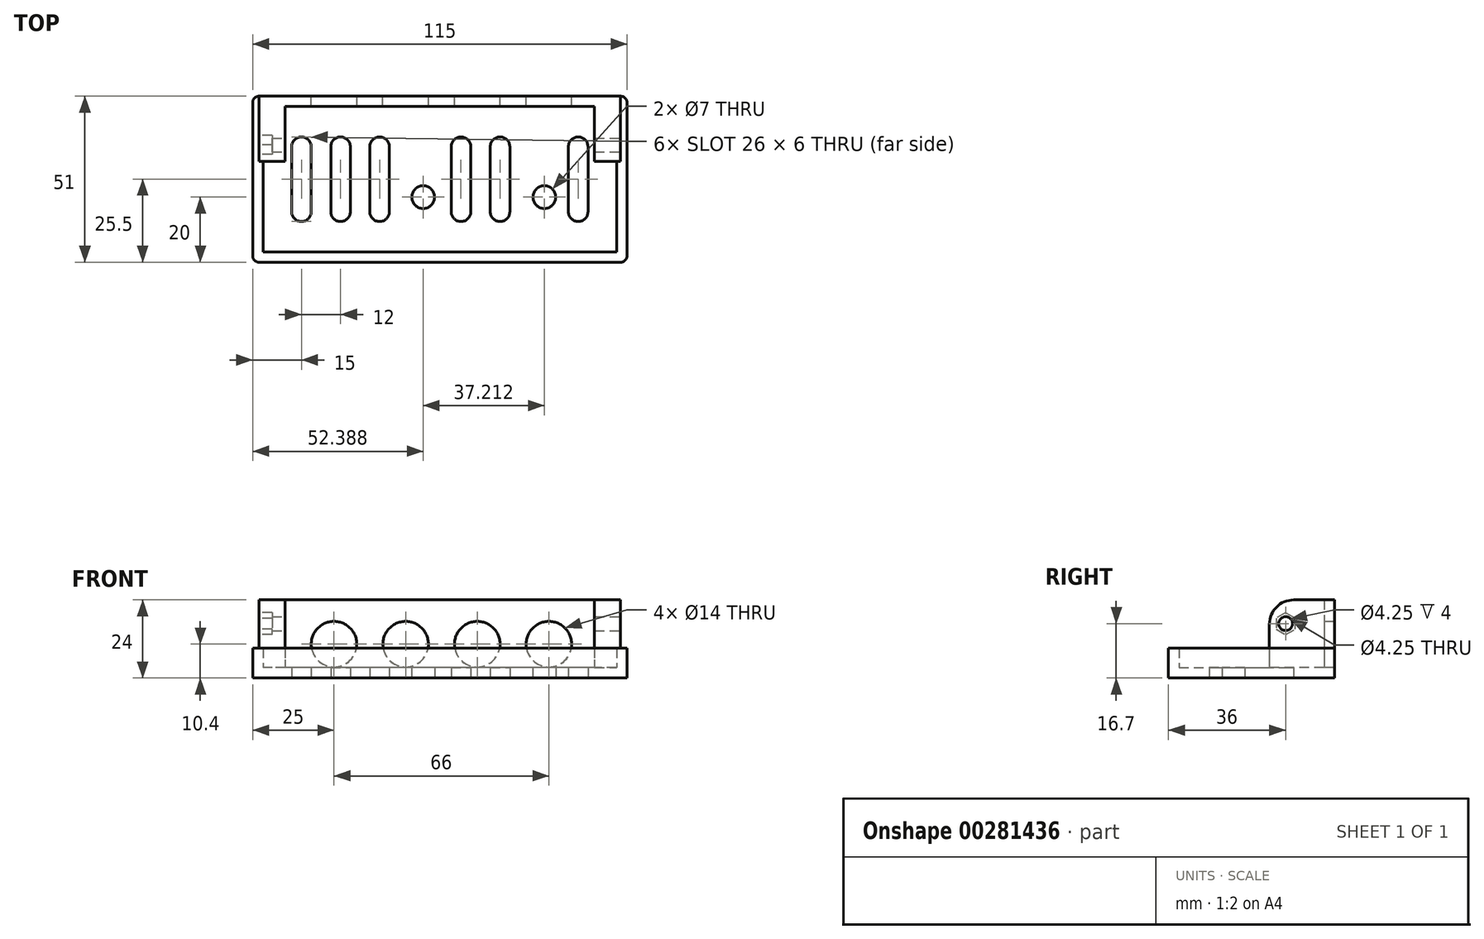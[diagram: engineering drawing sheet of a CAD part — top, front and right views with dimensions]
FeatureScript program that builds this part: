
annotation { "Feature Type Name" : "Feature", "Feature Type Description" : "" }
export const myFeature = defineFeature(function(context is Context, id is Id, definition is map)
    precondition{}
    {
        {
            var Q0;
            Q0=qCreatedBy(makeId("Top.planeOp"),FACE);
            var sketch = newSketch(context, id + "F0", { "sketchPlane" : qUnion([Q0])});
            skLineSegment(sketch, "E0.bottom", {"start": v(57.5, -25.5) * mm, "end": v(-57.5, -25.5) * mm});
            skLineSegment(sketch, "E0.top", {"start": v(57.5, 25.5) * mm, "end": v(-57.5, 25.5) * mm});
            skLineSegment(sketch, "E0.left", {"start": v(57.5, -25.5) * mm, "end": v(57.5, 25.5) * mm});
            skLineSegment(sketch, "E0.right", {"start": v(-57.5, -25.5) * mm, "end": v(-57.5, 25.5) * mm});
            skPoint(sketch, "E0.middle", {"position": v(0, 0) * mm});
            skLineSegment(sketch, "E1.bottom", {"start": v(-42.5, -13) * mm, "end": v(-42.5, -13) * mm});
            skLineSegment(sketch, "E1.top", {"start": v(-42.5, 13) * mm, "end": v(-42.5, 13) * mm});
            skLineSegment(sketch, "E1.left", {"start": v(-39.5, -10) * mm, "end": v(-39.5, 10) * mm});
            skLineSegment(sketch, "E1.right", {"start": v(-45.5, -10) * mm, "end": v(-45.5, 10) * mm});
            skPoint(sketch, "E1.middle", {"position": v(-42.5, 0) * mm});
            skLineSegment(sketch, "E2.bottom", {"start": v(-30.5, -13) * mm, "end": v(-30.5, -13) * mm});
            skLineSegment(sketch, "E2.top", {"start": v(-30.5, 13) * mm, "end": v(-30.5, 13) * mm});
            skLineSegment(sketch, "E2.left", {"start": v(-27.5, -10) * mm, "end": v(-27.5, 10) * mm});
            skLineSegment(sketch, "E2.right", {"start": v(-33.5, -10) * mm, "end": v(-33.5, 10) * mm});
            skPoint(sketch, "E2.middle", {"position": v(-30.5, 0) * mm});
            skLineSegment(sketch, "E3.bottom", {"start": v(-18.5, -13) * mm, "end": v(-18.5, -13) * mm});
            skLineSegment(sketch, "E3.top", {"start": v(-18.5, 13) * mm, "end": v(-18.5, 13) * mm});
            skLineSegment(sketch, "E3.left", {"start": v(-15.5, -10) * mm, "end": v(-15.5, 10) * mm});
            skLineSegment(sketch, "E3.right", {"start": v(-21.5, -10) * mm, "end": v(-21.5, 10) * mm});
            skPoint(sketch, "E3.middle", {"position": v(-18.5, 0) * mm});
            skLineSegment(sketch, "E4.bottom", {"start": v(6.5, -13) * mm, "end": v(6.5, -13) * mm});
            skLineSegment(sketch, "E4.top", {"start": v(6.5, 13) * mm, "end": v(6.5, 13) * mm});
            skLineSegment(sketch, "E4.left", {"start": v(9.5, -10) * mm, "end": v(9.5, 10) * mm});
            skLineSegment(sketch, "E4.right", {"start": v(3.5, -10) * mm, "end": v(3.5, 10) * mm});
            skPoint(sketch, "E4.middle", {"position": v(6.5, 0) * mm});
            skLineSegment(sketch, "E5.bottom", {"start": v(18.5, -13) * mm, "end": v(18.5, -13) * mm});
            skLineSegment(sketch, "E5.top", {"start": v(18.5, 13) * mm, "end": v(18.5, 13) * mm});
            skLineSegment(sketch, "E5.left", {"start": v(21.5, -10) * mm, "end": v(21.5, 10) * mm});
            skLineSegment(sketch, "E5.right", {"start": v(15.5, -10) * mm, "end": v(15.5, 10) * mm});
            skPoint(sketch, "E5.middle", {"position": v(18.5, 0) * mm});
            skLineSegment(sketch, "E6.bottom", {"start": v(42.5, -13) * mm, "end": v(42.5, -13) * mm});
            skLineSegment(sketch, "E6.top", {"start": v(42.5, 13) * mm, "end": v(42.5, 13) * mm});
            skLineSegment(sketch, "E6.left", {"start": v(45.5, -10) * mm, "end": v(45.5, 10) * mm});
            skLineSegment(sketch, "E6.right", {"start": v(39.5, -10) * mm, "end": v(39.5, 10) * mm});
            skPoint(sketch, "E6.middle", {"position": v(42.5, 0) * mm});
            skCircle(sketch, "E7", {"center": v(32.1, -5.5) * mm, "radius": 3.5 * mm});
            skCircle(sketch, "E8", {"center": v(-5.11, -5.5) * mm, "radius": 3.5 * mm});
            skPoint(sketch, "E9.visualSharp", {"position": v(-45.5, 13) * mm});
            skArc(sketch, "E9.filletArc", {"start": v(-42.5, 13) * mm, "mid": v(-44.62, 12.12) * mm, "end": v(-45.5, 10) * mm});
            skPoint(sketch, "E10.visualSharp", {"position": v(-39.5, 13) * mm});
            skArc(sketch, "E10.filletArc", {"start": v(-39.5, 10) * mm, "mid": v(-40.38, 12.12) * mm, "end": v(-42.5, 13) * mm});
            skPoint(sketch, "E11.visualSharp", {"position": v(-39.5, -13) * mm});
            skArc(sketch, "E11.filletArc", {"start": v(-42.5, -13) * mm, "mid": v(-40.38, -12.12) * mm, "end": v(-39.5, -10) * mm});
            skPoint(sketch, "E12.visualSharp", {"position": v(-45.5, -13) * mm});
            skArc(sketch, "E12.filletArc", {"start": v(-45.5, -10) * mm, "mid": v(-44.62, -12.12) * mm, "end": v(-42.5, -13) * mm});
            skPoint(sketch, "E13.visualSharp", {"position": v(-33.5, -13) * mm});
            skArc(sketch, "E13.filletArc", {"start": v(-33.5, -10) * mm, "mid": v(-32.62, -12.12) * mm, "end": v(-30.5, -13) * mm});
            skPoint(sketch, "E14.visualSharp", {"position": v(-27.5, -13) * mm});
            skArc(sketch, "E14.filletArc", {"start": v(-30.5, -13) * mm, "mid": v(-28.38, -12.12) * mm, "end": v(-27.5, -10) * mm});
            skPoint(sketch, "E15.visualSharp", {"position": v(-27.5, 13) * mm});
            skArc(sketch, "E15.filletArc", {"start": v(-27.5, 10) * mm, "mid": v(-28.38, 12.12) * mm, "end": v(-30.5, 13) * mm});
            skPoint(sketch, "E16.visualSharp", {"position": v(-33.5, 13) * mm});
            skArc(sketch, "E16.filletArc", {"start": v(-30.5, 13) * mm, "mid": v(-32.62, 12.12) * mm, "end": v(-33.5, 10) * mm});
            skPoint(sketch, "E17.visualSharp", {"position": v(-21.5, 13) * mm});
            skArc(sketch, "E17.filletArc", {"start": v(-18.5, 13) * mm, "mid": v(-20.62, 12.12) * mm, "end": v(-21.5, 10) * mm});
            skPoint(sketch, "E18.visualSharp", {"position": v(-15.5, 13) * mm});
            skArc(sketch, "E18.filletArc", {"start": v(-15.5, 10) * mm, "mid": v(-16.38, 12.12) * mm, "end": v(-18.5, 13) * mm});
            skPoint(sketch, "E19.visualSharp", {"position": v(-15.5, -13) * mm});
            skArc(sketch, "E19.filletArc", {"start": v(-18.5, -13) * mm, "mid": v(-16.38, -12.12) * mm, "end": v(-15.5, -10) * mm});
            skPoint(sketch, "E20.visualSharp", {"position": v(-21.5, -13) * mm});
            skArc(sketch, "E20.filletArc", {"start": v(-21.5, -10) * mm, "mid": v(-20.62, -12.12) * mm, "end": v(-18.5, -13) * mm});
            skPoint(sketch, "E21.visualSharp", {"position": v(3.5, -13) * mm});
            skArc(sketch, "E21.filletArc", {"start": v(3.5, -10) * mm, "mid": v(4.38, -12.12) * mm, "end": v(6.5, -13) * mm});
            skPoint(sketch, "E22.visualSharp", {"position": v(9.5, -13) * mm});
            skArc(sketch, "E22.filletArc", {"start": v(6.5, -13) * mm, "mid": v(8.62, -12.12) * mm, "end": v(9.5, -10) * mm});
            skPoint(sketch, "E23.visualSharp", {"position": v(9.5, 13) * mm});
            skArc(sketch, "E23.filletArc", {"start": v(9.5, 10) * mm, "mid": v(8.62, 12.12) * mm, "end": v(6.5, 13) * mm});
            skPoint(sketch, "E24.visualSharp", {"position": v(3.5, 13) * mm});
            skArc(sketch, "E24.filletArc", {"start": v(6.5, 13) * mm, "mid": v(4.38, 12.12) * mm, "end": v(3.5, 10) * mm});
            skPoint(sketch, "E25.visualSharp", {"position": v(15.5, -13) * mm});
            skArc(sketch, "E25.filletArc", {"start": v(15.5, -10) * mm, "mid": v(16.38, -12.12) * mm, "end": v(18.5, -13) * mm});
            skPoint(sketch, "E26.visualSharp", {"position": v(21.5, -13) * mm});
            skArc(sketch, "E26.filletArc", {"start": v(18.5, -13) * mm, "mid": v(20.62, -12.12) * mm, "end": v(21.5, -10) * mm});
            skPoint(sketch, "E27.visualSharp", {"position": v(21.5, 13) * mm});
            skArc(sketch, "E27.filletArc", {"start": v(21.5, 10) * mm, "mid": v(20.62, 12.12) * mm, "end": v(18.5, 13) * mm});
            skPoint(sketch, "E28.visualSharp", {"position": v(15.5, 13) * mm});
            skArc(sketch, "E28.filletArc", {"start": v(18.5, 13) * mm, "mid": v(16.38, 12.12) * mm, "end": v(15.5, 10) * mm});
            skPoint(sketch, "E29.visualSharp", {"position": v(39.5, -13) * mm});
            skArc(sketch, "E29.filletArc", {"start": v(39.5, -10) * mm, "mid": v(40.38, -12.12) * mm, "end": v(42.5, -13) * mm});
            skPoint(sketch, "E30.visualSharp", {"position": v(45.5, 13) * mm});
            skArc(sketch, "E30.filletArc", {"start": v(45.5, 10) * mm, "mid": v(44.62, 12.12) * mm, "end": v(42.5, 13) * mm});
            skPoint(sketch, "E31.visualSharp", {"position": v(39.5, 13) * mm});
            skArc(sketch, "E31.filletArc", {"start": v(42.5, 13) * mm, "mid": v(40.38, 12.12) * mm, "end": v(39.5, 10) * mm});
            skPoint(sketch, "E32.visualSharp", {"position": v(45.5, -13) * mm});
            skArc(sketch, "E32.filletArc", {"start": v(42.5, -13) * mm, "mid": v(44.62, -12.12) * mm, "end": v(45.5, -10) * mm});
            skSolve(sketch);
        }
        {
            var Q0;
            Q0=qSketchRegion(id+"F0",true);
            extrude(context, id + "F1", {"entities" : qUnion([Q0]), "depth" : 3.2 * mm});
        }
        {
            var Q0;
            Q0=makeQuery(id+"F1.opExtrude","CAP_FACE",FACE,{"disambiguationData":[OSD([sQuery(id+"F0.wireOp",EDGE,"E0.bottom"),sQuery(id+"F0.wireOp",EDGE,"E0.top"),sQuery(id+"F0.wireOp",EDGE,"E0.left"),sQuery(id+"F0.wireOp",EDGE,"E0.right"),sQuery(id+"F0.wireOp",EDGE,"E1.bottom"),sQuery(id+"F0.wireOp",EDGE,"E1.top"),sQuery(id+"F0.wireOp",EDGE,"E1.left"),sQuery(id+"F0.wireOp",EDGE,"E1.right"),sQuery(id+"F0.wireOp",EDGE,"E2.bottom"),sQuery(id+"F0.wireOp",EDGE,"E2.top"),sQuery(id+"F0.wireOp",EDGE,"E2.left"),sQuery(id+"F0.wireOp",EDGE,"E2.right"),sQuery(id+"F0.wireOp",EDGE,"E3.bottom"),sQuery(id+"F0.wireOp",EDGE,"E3.top"),sQuery(id+"F0.wireOp",EDGE,"E3.left"),sQuery(id+"F0.wireOp",EDGE,"E3.right"),sQuery(id+"F0.wireOp",EDGE,"E4.bottom"),sQuery(id+"F0.wireOp",EDGE,"E4.top"),sQuery(id+"F0.wireOp",EDGE,"E4.left"),sQuery(id+"F0.wireOp",EDGE,"E4.right"),sQuery(id+"F0.wireOp",EDGE,"E5.bottom"),sQuery(id+"F0.wireOp",EDGE,"E5.top"),sQuery(id+"F0.wireOp",EDGE,"E5.left"),sQuery(id+"F0.wireOp",EDGE,"E5.right"),sQuery(id+"F0.wireOp",EDGE,"E6.bottom"),sQuery(id+"F0.wireOp",EDGE,"E6.top"),sQuery(id+"F0.wireOp",EDGE,"E6.left"),sQuery(id+"F0.wireOp",EDGE,"E6.right"),sQuery(id+"F0.wireOp",EDGE,"E7"),sQuery(id+"F0.wireOp",EDGE,"E8")])],"isStart":true});
            var sketch = newSketch(context, id + "F2", { "sketchPlane" : qUnion([Q0])});
            skLineSegment(sketch, "E33", {"start": v(-55.5, -5.5) * mm, "end": v(-55.5, -25.5) * mm});
            skLineSegment(sketch, "E34", {"start": v(-55.5, -25.5) * mm, "end": v(55.5, -25.5) * mm});
            skLineSegment(sketch, "E35", {"start": v(55.5, -25.5) * mm, "end": v(55.5, -5.5) * mm});
            skLineSegment(sketch, "E36", {"start": v(55.5, -5.5) * mm, "end": v(47.5, -5.5) * mm});
            skLineSegment(sketch, "E37", {"start": v(47.5, -5.5) * mm, "end": v(47.5, -22.3) * mm});
            skLineSegment(sketch, "E38", {"start": v(-55.5, -5.5) * mm, "end": v(-47.5, -5.5) * mm});
            skLineSegment(sketch, "E39", {"start": v(-47.5, -5.5) * mm, "end": v(-47.5, -22.3) * mm});
            skLineSegment(sketch, "E40", {"start": v(-47.5, -22.3) * mm, "end": v(47.5, -22.3) * mm});
            skSolve(sketch);
        }
        {
            var Q0;
            Q0=qSketchRegion(id+"F2",true);
            extrude(context, id + "F3", {"entities" : qUnion([Q0]), "operationType" : NewBodyOperationType.ADD, "oppositeDirection" : true, "depth" : 24 * mm});
        }
        {
            var Q0;
            Q0=makeQuery(id+"F1.opExtrude","CAP_FACE",FACE,{"disambiguationData":[OSD([sQuery(id+"F0.wireOp",EDGE,"E0.bottom"),sQuery(id+"F0.wireOp",EDGE,"E0.top"),sQuery(id+"F0.wireOp",EDGE,"E0.left"),sQuery(id+"F0.wireOp",EDGE,"E0.right"),sQuery(id+"F0.wireOp",EDGE,"E1.left"),sQuery(id+"F0.wireOp",EDGE,"E1.right"),sQuery(id+"F0.wireOp",EDGE,"E2.left"),sQuery(id+"F0.wireOp",EDGE,"E2.right"),sQuery(id+"F0.wireOp",EDGE,"E3.left"),sQuery(id+"F0.wireOp",EDGE,"E3.right"),sQuery(id+"F0.wireOp",EDGE,"E4.left"),sQuery(id+"F0.wireOp",EDGE,"E4.right"),sQuery(id+"F0.wireOp",EDGE,"E5.left"),sQuery(id+"F0.wireOp",EDGE,"E5.right"),sQuery(id+"F0.wireOp",EDGE,"E6.left"),sQuery(id+"F0.wireOp",EDGE,"E6.right"),sQuery(id+"F0.wireOp",EDGE,"E7"),sQuery(id+"F0.wireOp",EDGE,"E8"),sQuery(id+"F0.wireOp",EDGE,"E9.filletArc"),sQuery(id+"F0.wireOp",EDGE,"E10.filletArc"),sQuery(id+"F0.wireOp",EDGE,"E11.filletArc"),sQuery(id+"F0.wireOp",EDGE,"E12.filletArc"),sQuery(id+"F0.wireOp",EDGE,"E13.filletArc"),sQuery(id+"F0.wireOp",EDGE,"E14.filletArc"),sQuery(id+"F0.wireOp",EDGE,"E15.filletArc"),sQuery(id+"F0.wireOp",EDGE,"E16.filletArc"),sQuery(id+"F0.wireOp",EDGE,"E17.filletArc"),sQuery(id+"F0.wireOp",EDGE,"E18.filletArc"),sQuery(id+"F0.wireOp",EDGE,"E19.filletArc"),sQuery(id+"F0.wireOp",EDGE,"E20.filletArc"),sQuery(id+"F0.wireOp",EDGE,"E21.filletArc"),sQuery(id+"F0.wireOp",EDGE,"E22.filletArc"),sQuery(id+"F0.wireOp",EDGE,"E23.filletArc"),sQuery(id+"F0.wireOp",EDGE,"E24.filletArc"),sQuery(id+"F0.wireOp",EDGE,"E25.filletArc"),sQuery(id+"F0.wireOp",EDGE,"E26.filletArc"),sQuery(id+"F0.wireOp",EDGE,"E27.filletArc"),sQuery(id+"F0.wireOp",EDGE,"E28.filletArc"),sQuery(id+"F0.wireOp",EDGE,"E29.filletArc"),sQuery(id+"F0.wireOp",EDGE,"E30.filletArc"),sQuery(id+"F0.wireOp",EDGE,"E31.filletArc"),sQuery(id+"F0.wireOp",EDGE,"E32.filletArc")])],"isStart":false});
            var sketch = newSketch(context, id + "F4", { "sketchPlane" : qUnion([Q0])});
            skLineSegment(sketch, "E41", {"start": v(-55.5, 25.5) * mm, "end": v(-57.5, 25.5) * mm});
            skLineSegment(sketch, "E42", {"start": v(-57.5, 25.5) * mm, "end": v(-57.5, -25.5) * mm});
            skLineSegment(sketch, "E43", {"start": v(-57.5, -25.5) * mm, "end": v(57.5, -25.5) * mm});
            skLineSegment(sketch, "E44", {"start": v(57.5, -25.5) * mm, "end": v(57.5, 25.5) * mm});
            skLineSegment(sketch, "E45", {"start": v(57.5, 25.5) * mm, "end": v(55.5, 25.5) * mm});
            skLineSegment(sketch, "E46", {"start": v(55.5, 25.5) * mm, "end": v(55.5, 5.5) * mm});
            skLineSegment(sketch, "E47", {"start": v(55.5, 5.5) * mm, "end": v(54.3, 5.5) * mm});
            skLineSegment(sketch, "E48", {"start": v(54.3, 5.5) * mm, "end": v(54.3, -22.3) * mm});
            skLineSegment(sketch, "E49", {"start": v(54.3, -22.3) * mm, "end": v(-54.3, -22.3) * mm});
            skLineSegment(sketch, "E50", {"start": v(-54.3, -22.3) * mm, "end": v(-54.3, 5.5) * mm});
            skLineSegment(sketch, "E51", {"start": v(-54.3, 5.5) * mm, "end": v(-55.5, 5.5) * mm});
            skLineSegment(sketch, "E52", {"start": v(-55.5, 5.5) * mm, "end": v(-55.5, 25.5) * mm});
            skLineSegment(sketch, "E53", {"start": v(54.3, 5.5) * mm, "end": v(55.5, 5.5) * mm});
            skSolve(sketch);
        }
        {
            var Q0;
            Q0=qSketchRegion(id+"F4",true);
            extrude(context, id + "F5", {"entities" : qUnion([Q0]), "operationType" : NewBodyOperationType.ADD, "depth" : 6 * mm});
        }
        {
            var Q0;
            Q0=makeQuery(id+"F3.opExtrude","SWEPT_FACE",FACE,{"disambiguationData":[OSD([sQuery(id+"F2.wireOp",EDGE,"E35")])]});
            var sketch = newSketch(context, id + "F6", { "sketchPlane" : qUnion([Q0])});
            skCircle(sketch, "E54", {"center": v(10.5, 16.7) * mm, "radius": 2.12 * mm});
            skSolve(sketch);
        }
        {
            var Q0;
            Q0=qSketchRegion(id+"F6",true);
            extrude(context, id + "F7", {"entities" : qUnion([Q0]), "operationType" : NewBodyOperationType.REMOVE, "endBound" : BoundingType.THROUGH_ALL, "oppositeDirection" : true, "depth" : 25 * mm});
        }
        {
            var Q0;
            Q0=makeQuery(id+"F3.opExtrude","CAP_EDGE",EDGE,{"disambiguationData":[OSD([sQuery(id+"F2.wireOp",EDGE,"E36")])],"isStart":false});
            var Q1;
            Q1=makeQuery(id+"F3.opExtrude","CAP_EDGE",EDGE,{"disambiguationData":[OSD([sQuery(id+"F2.wireOp",EDGE,"E38")])],"isStart":false});
            fillet(context, id + "F8", {"entities" : qUnion([Q0, Q1]), "radius" : 7.5 * mm, "tangentPropagation" : true, "allowEdgeOverflow" : false});
        }
        {
            var Q0;
            Q0=makeQuery(id+"F5.boolean.opBoolean","MERGE",EDGE,{"derivedFrom":[makeQuery(id+"F1.opExtrude","SWEPT_EDGE",EDGE,{"disambiguationData":[OSD([sQuery(id+"F0.wireOp",EDGE,"E0.bottom"),sQuery(id+"F0.wireOp",EDGE,"E0.right")])]}),makeQuery(id+"F5.opExtrude","SWEPT_EDGE",EDGE,{"disambiguationData":[OSD([sQuery(id+"F4.wireOp",EDGE,"E42"),sQuery(id+"F4.wireOp",EDGE,"E43")])]})]});
            var Q1;
            Q1=makeQuery(id+"F5.boolean.opBoolean","MERGE",EDGE,{"derivedFrom":[makeQuery(id+"F1.opExtrude","SWEPT_EDGE",EDGE,{"disambiguationData":[OSD([sQuery(id+"F0.wireOp",EDGE,"E0.bottom"),sQuery(id+"F0.wireOp",EDGE,"E0.left")])]}),makeQuery(id+"F5.opExtrude","SWEPT_EDGE",EDGE,{"disambiguationData":[OSD([sQuery(id+"F4.wireOp",EDGE,"E43"),sQuery(id+"F4.wireOp",EDGE,"E44")])]})]});
            var Q2;
            Q2=makeQuery(id+"F5.boolean.opBoolean","MERGE",EDGE,{"derivedFrom":[makeQuery(id+"F1.opExtrude","SWEPT_EDGE",EDGE,{"disambiguationData":[OSD([sQuery(id+"F0.wireOp",EDGE,"E0.top"),sQuery(id+"F0.wireOp",EDGE,"E0.left")])]}),makeQuery(id+"F5.opExtrude","SWEPT_EDGE",EDGE,{"disambiguationData":[OSD([sQuery(id+"F4.wireOp",EDGE,"E44"),sQuery(id+"F4.wireOp",EDGE,"E45")])]})]});
            var Q3;
            Q3=makeQuery(id+"F5.boolean.opBoolean","MERGE",EDGE,{"derivedFrom":[makeQuery(id+"F1.opExtrude","SWEPT_EDGE",EDGE,{"disambiguationData":[OSD([sQuery(id+"F0.wireOp",EDGE,"E0.top"),sQuery(id+"F0.wireOp",EDGE,"E0.right")])]}),makeQuery(id+"F5.opExtrude","SWEPT_EDGE",EDGE,{"disambiguationData":[OSD([sQuery(id+"F4.wireOp",EDGE,"E41"),sQuery(id+"F4.wireOp",EDGE,"E42")])]})]});
            fillet(context, id + "F9", {"entities" : qUnion([Q0, Q1, Q2, Q3]), "radius" : 2 * mm, "tangentPropagation" : true, "allowEdgeOverflow" : false});
        }
        {
            var Q0;
            Q0=makeQuery(id+"F5.boolean.opBoolean","MERGE",FACE,{"derivedFrom":[makeQuery(id+"F3.boolean.opBoolean","MERGE",FACE,{"derivedFrom":[makeQuery(id+"F1.opExtrude","SWEPT_FACE",FACE,{"disambiguationData":[OSD([sQuery(id+"F0.wireOp",EDGE,"E0.top")])]}),makeQuery(id+"F3.opExtrude","SWEPT_FACE",FACE,{"disambiguationData":[OSD([sQuery(id+"F2.wireOp",EDGE,"E34")])]})]}),makeQuery(id+"F5.opExtrude","SWEPT_FACE",FACE,{"disambiguationData":[OSD([sQuery(id+"F4.wireOp",EDGE,"E41")])]}),makeQuery(id+"F5.opExtrude","SWEPT_FACE",FACE,{"disambiguationData":[OSD([sQuery(id+"F4.wireOp",EDGE,"E45")])]})]});
            var sketch = newSketch(context, id + "F10", { "sketchPlane" : qUnion([Q0])});
            skCircle(sketch, "E55", {"center": v(-33.5, 10.4) * mm, "radius": 7 * mm});
            skCircle(sketch, "E56.1.0.0", {"center": v(-11.5, 10.4) * mm, "radius": 7 * mm});
            skCircle(sketch, "E56.2.0.0", {"center": v(10.5, 10.4) * mm, "radius": 7 * mm});
            skCircle(sketch, "E56.3.0.0", {"center": v(32.5, 10.4) * mm, "radius": 7 * mm});
            skLineSegment(sketch, "E56.direction1", {"start": v(-33.5, 10.4) * mm, "end": v(-11.5, 10.4) * mm, "construction": true});
            skSolve(sketch);
        }
        {
            var Q0;
            Q0=qSketchRegion(id+"F10",true);
            extrude(context, id + "F11", {"entities" : qUnion([Q0]), "operationType" : NewBodyOperationType.REMOVE, "oppositeDirection" : true, "depth" : 5 * mm});
        }
        {
            var Q0;
            Q0=makeQuery(id+"F3.opExtrude","SWEPT_FACE",FACE,{"disambiguationData":[OSD([sQuery(id+"F2.wireOp",EDGE,"E33")])]});
            var sketch = newSketch(context, id + "F12", { "sketchPlane" : qUnion([Q0])});
            skCircle(sketch, "E57.cCircle", {"center": v(-10.5, 16.7) * mm, "radius": 2.93 * mm, "construction": true});
            skLineSegment(sketch, "E57.0", {"start": v(-7.57, 18.39) * mm, "end": v(-7.57, 15.01) * mm});
            skLineSegment(sketch, "E57.1", {"start": v(-7.57, 15.01) * mm, "end": v(-10.5, 13.32) * mm});
            skLineSegment(sketch, "E57.2", {"start": v(-10.5, 13.32) * mm, "end": v(-13.42, 15.01) * mm});
            skLineSegment(sketch, "E57.3", {"start": v(-13.42, 15.01) * mm, "end": v(-13.42, 18.39) * mm});
            skLineSegment(sketch, "E57.4", {"start": v(-13.42, 18.39) * mm, "end": v(-10.5, 20.08) * mm});
            skLineSegment(sketch, "E57.5", {"start": v(-10.5, 20.08) * mm, "end": v(-7.57, 18.39) * mm});
            skPoint(sketch, "E57.0.midPoint", {"position": v(-7.57, 16.7) * mm});
            skSolve(sketch);
        }
        {
            var Q0;
            Q0=qSketchRegion(id+"F12",true);
            extrude(context, id + "F13", {"entities" : qUnion([Q0]), "operationType" : NewBodyOperationType.REMOVE, "oppositeDirection" : true, "depth" : 4 * mm});
        }
    });
